# Revit family: Monkey Toe Sky Walkway (Non-Levelled)
name_source: partatom
category: Mechanical Equipment
revit_build: Autodesk Revit 2016 (Build: 20150714_1515(x64)
units: mm (PartAtom-declared; Revit-internal decimal feet)

## family parameters
Always vertical = No
Cut with Voids When Loaded = No
Host = Roof
Part Type = Normal
Room Calculation Point = No
Round Connector Dimension = Use Diameter
Shared = No
Work Plane-Based = No

## types (2) — shared parameters
Manufacturer = Monkey Toe Systems Limited
Model = SKYWALK WALKWAY (NON LEVELLED, ON SAME ANGLE OF ROOF)
Monkey Toe Grating = <By Category>
Monkey Toe Steel = <By Category>
Railing (Right) = No
Railing (Support) = No
URL = http://www.monkeytoe.co.nz

## per-type parameters (varying)
| type | Description |
| Premium Walkway (Along Slope) | "SKYWALK WALKWAY (NON LEVELLED, ON SAME ANGLE OF ROOF)" |
| Sky Walkway (Against Slope) |  |

## geometry (parser evidence)
native form markers: Extrusion x7, Sweep x50
no freeform markers — native parametric forms only
